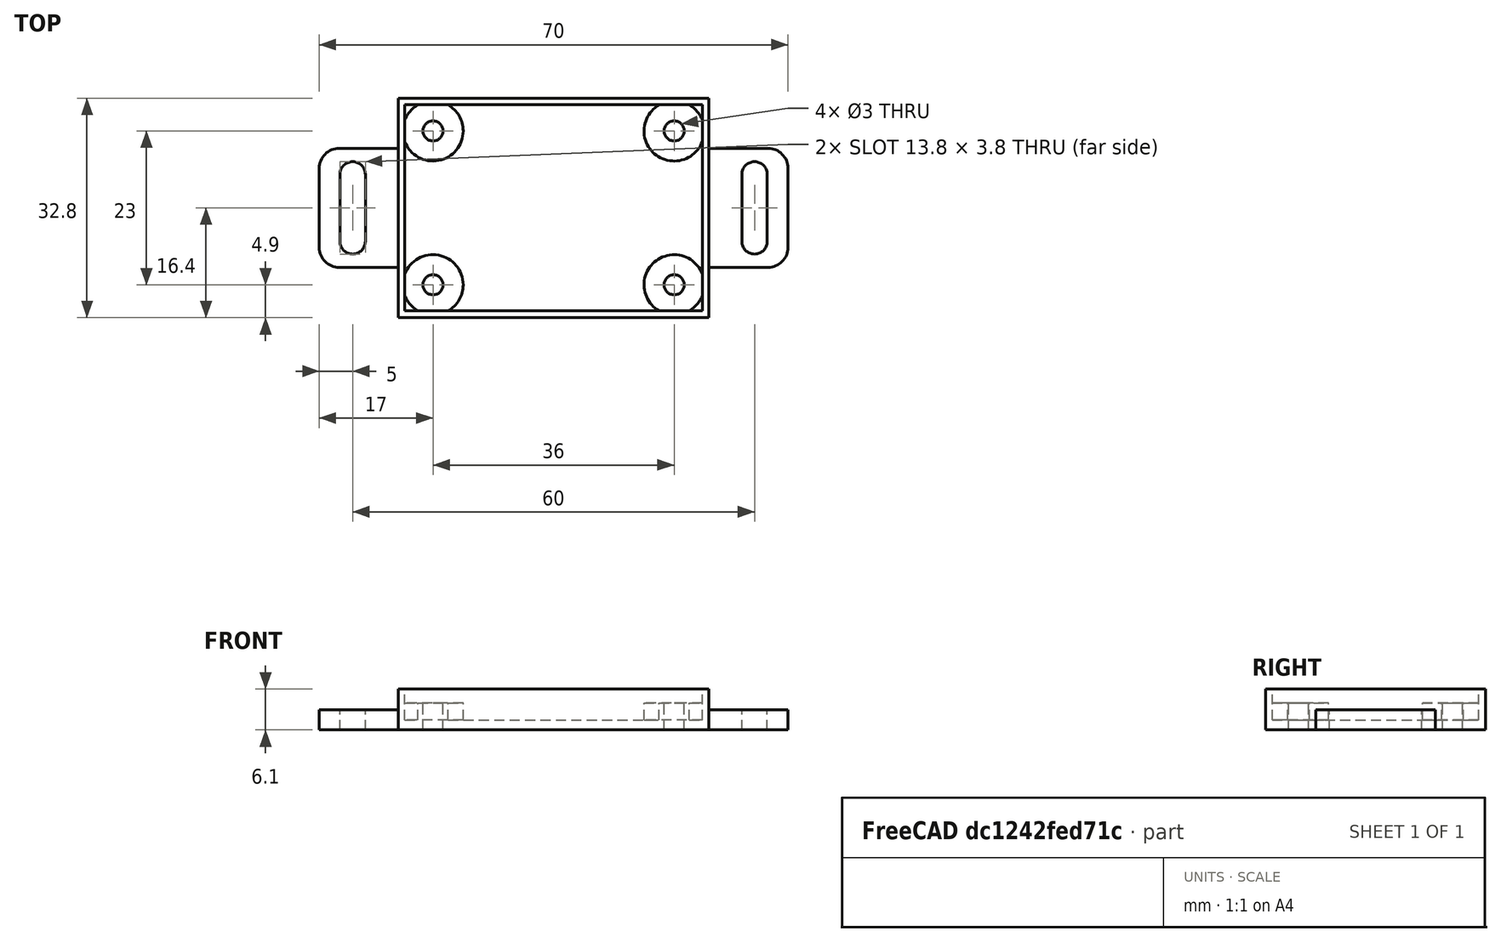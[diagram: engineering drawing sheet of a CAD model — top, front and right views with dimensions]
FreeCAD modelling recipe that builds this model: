
FCSTD DOCUMENT  (FreeCAD 0.18.4R)
Label: step_down_rect
License: FreeArt
LicenseURL: http://artlibre.org/licence/lal
objects: Part::Box×2, Part::Cylinder×2, Part::FeaturePython×2, Part::MultiFuse×2, Part::Cut×2, Spreadsheet::Sheet×1, Part::Feature×1
note: 11 computed .brp shape members not serialized (recipe doc carries the construction recipe); baked Part::Feature solids carry a one-line shape summary decoded from their .brp

FEATURE [Part::Box] Box  label="outer cube"
  AttacherType = Attacher::AttachEngine3D
  Height = 6.1
  Length = 46.4
  Width = 32.8
  expr: Height = p.box_z
  expr: Width = p.box_y
  expr: Length = p.box_x
FEATURE [Spreadsheet::Sheet] Spreadsheet  label="p"
  cells = A1=hole_dist_x; B1(hole_dist_x)=36; A2=hole_dist_y; B2(hole_dist_y)=23; A3=hole_r; B3(hole_r)=1.5; A4=hole_wall; B4(hole_wall)=3; A5=pcb_x; B5(pcb_x)=44.4; A6=pcb_y; B6(pcb_y)=30.8; A7=pcb_z; B7(pcb_z)=1.6; A8=pcb_under; B8(pcb_under)=2.5; A9=side_wall; B9(side_wall)=1; A10=bottom_wall; B10(bottom_wall)=1.5; A11=box_x; B11(box_x)==p.pcb_x + 2 * p.side_wall; A12=box_y; B12(box_y)==p.pcb_y + 2 * p.side_wall; A13=box_z; B13(box_z)==p.pcb_under + p.pcb_z + p.bottom_wall
FEATURE [Part::Box] Box001  label="extraction cube"
  AttacherType = Attacher::AttachEngine3D
  Height = 20
  Length = 44.4
  Placement = pos=(1,1,1.5) rot=(0,0,1;0rad)
  Width = 30.8
  expr: Placement.Base.z = p.bottom_wall
  expr: Placement.Base.y = p.side_wall
  expr: Placement.Base.x = p.side_wall
  expr: Width = p.pcb_y
  expr: Length = p.pcb_x
FEATURE [Part::Cylinder] Cylinder  label="hole"
  Angle = 360
  AttacherType = Attacher::AttachEngine3D
  Height = 10
  Radius = 1.5
  expr: Radius = p.hole_r
FEATURE [Part::FeaturePython] Array  label="hole array"  # Draft array (typed FeaturePython)
  Angle = 360
  ArrayType = 0
  Axis = (0,0,1)
  Base = -> Cylinder
  Center = (0,0,0)
  Fuse = false
  IntervalAxis = (0,0,0)
  IntervalX = (36,0,0)
  IntervalY = (0,23,0)
  IntervalZ = (0,0,1)
  NumberPolar = 1
  NumberX = 2
  NumberY = 2
  NumberZ = 1
  Placement = pos=(5.2,4.9,0) rot=(0,0,1;0rad)
  expr: Placement.Base.y = (p.box_y - p.hole_dist_y) / 2
  expr: Placement.Base.x = (p.box_x - p.hole_dist_x) / 2
  expr: IntervalY.y = p.hole_dist_y
  expr: IntervalX.x = p.hole_dist_x
FEATURE [Part::Cylinder] Cylinder001  label="hole wall"
  Angle = 360
  AttacherType = Attacher::AttachEngine3D
  Height = 4
  Radius = 4.5
  expr: Height = p.bottom_wall + p.pcb_under
  expr: Radius = p.hole_r + p.hole_wall
FEATURE [Part::FeaturePython] Array001  label="hole wall array"  # Draft array (typed FeaturePython)
  Angle = 360
  ArrayType = 0
  Axis = (0,0,1)
  Base = -> Cylinder001
  Center = (0,0,0)
  Fuse = false
  IntervalAxis = (0,0,0)
  IntervalX = (36,0,0)
  IntervalY = (0,23,0)
  IntervalZ = (0,0,1)
  NumberPolar = 1
  NumberX = 2
  NumberY = 2
  NumberZ = 1
  Placement = pos=(5.2,4.9,0) rot=(0,0,1;0rad)
  expr: Placement.Base.y = (p.box_y - p.hole_dist_y) / 2
  expr: Placement.Base.x = (p.box_x - p.hole_dist_x) / 2
  expr: IntervalY.y = p.hole_dist_y
  expr: IntervalX.x = p.hole_dist_x
FEATURE [Part::Feature] Cut003001  label="attach plane x dir"
  shape: bbox 70 x 17.8 x 3 mm, 18 faces (baked)
FEATURE [Part::MultiFuse] Fusion001  label="box fusion"
  Shapes = -> [Box,Cut003001]
FEATURE [Part::Cut] Cut  label="step down box cut"
  Base = -> Fusion001
  Tool = -> Box001
FEATURE [Part::MultiFuse] Fusion002  label="box fusion002"
  Shapes = -> [Cut,Array001]
FEATURE [Part::Cut] Cut003002  label="box cut"
  Base = -> Fusion002
  Tool = -> Array
